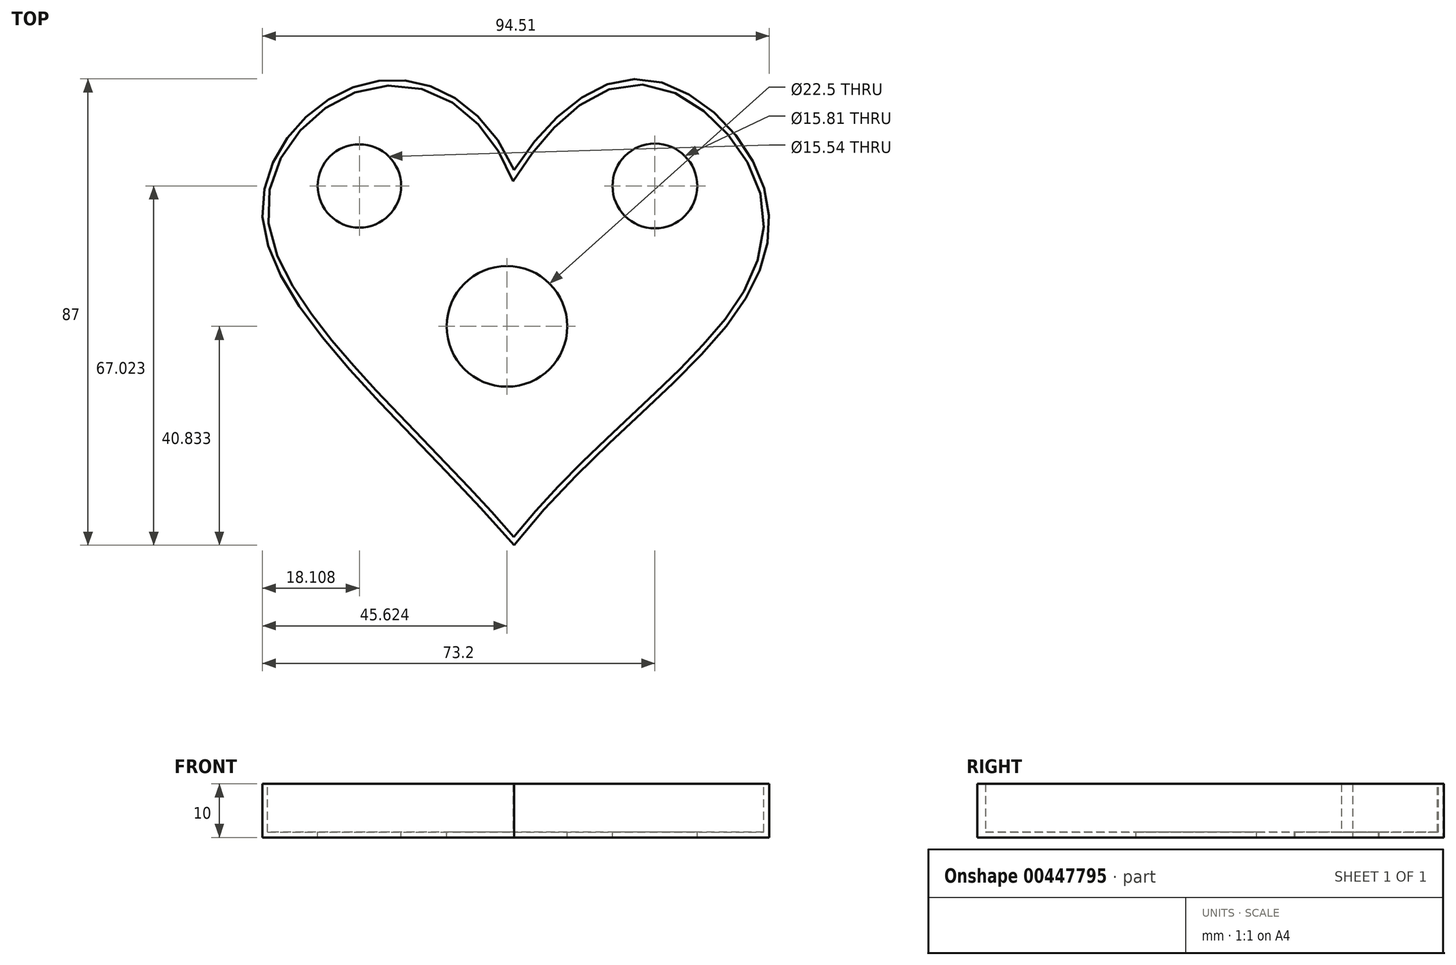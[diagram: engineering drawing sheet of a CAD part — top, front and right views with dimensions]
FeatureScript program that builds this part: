
annotation { "Feature Type Name" : "Feature", "Feature Type Description" : "" }
export const myFeature = defineFeature(function(context is Context, id is Id, definition is map)
    precondition{}
    {
        {
            var Q0;
            Q0=qCreatedBy(makeId("Top.planeOp"),FACE);
            var sketch = newSketch(context, id + "F0", { "sketchPlane" : qUnion([Q0])});
            skFitSpline(sketch, "E0", {"points": [v(0, 16.97) * mm, v(-27.58, 33.14) * mm, v(-46.93, 8.75) * mm, v(0, -53.03) * mm], "startDerivative": vector(-62.03, 140.99) * mm, "endDerivative": vector(141.18, -162.9) * mm});
            skFitSpline(sketch, "E1", {"points": [v(0, -53.03) * mm, v(41.9, -9.02) * mm, v(45.6, 16.44) * mm, v(23.86, 33.94) * mm, v(0, 16.97) * mm], "startDerivative": vector(122.52, 158.56) * mm, "endDerivative": vector(-83.12, -128.15) * mm});
            skSolve(sketch);
        }
        {
            var Q0;
            Q0=makeQuery(id+"F0.imprint","IMPRINT",FACE,{"disambiguationData":[TD([[makeQuery(id+"F0.imprint","IMPRINT",EDGE,{"derivedFrom":sQuery(id+"F0.wireOp",EDGE,"E0")}),1.0]])]});
            extrude(context, id + "F1", {"entities" : qUnion([Q0]), "depth" : 10 * mm});
        }
        {
            var Q0;
            Q0=makeQuery(id+"F1.opExtrude","CAP_FACE",FACE,{"disambiguationData":[OSD([sQuery(id+"F0.wireOp",EDGE,"E0"),sQuery(id+"F0.wireOp",EDGE,"E1")])],"isStart":false});
            shell(context, id + "F2", {"entities" : qUnion([Q0]), "thickness" : 1 * mm});
        }
        {
            var Q0;
            Q0=makeQuery(id+"F2.opShell","OFFSET_FACE",FACE,{"disambiguationData":[OSD([sQuery(id+"F0.wireOp",EDGE,"E0"),sQuery(id+"F0.wireOp",EDGE,"E1")])]});
            var sketch = newSketch(context, id + "F3", { "sketchPlane" : qUnion([Q0])});
            skCircle(sketch, "E2", {"center": v(-28.84, 14) * mm, "radius": 7.77 * mm});
            skCircle(sketch, "E3", {"center": v(-1.33, -12.2) * mm, "radius": 11.25 * mm});
            skCircle(sketch, "E4", {"center": v(26.25, 14) * mm, "radius": 7.9 * mm});
            skSolve(sketch);
        }
        {
            var Q0;
            Q0=makeQuery(id+"F3.imprint","IMPRINT",FACE,{"disambiguationData":[TD([[makeQuery(id+"F3.imprint","IMPRINT",EDGE,{"derivedFrom":sQuery(id+"F3.wireOp",EDGE,"E2")}),1.0]])]});
            var Q1;
            Q1=makeQuery(id+"F3.imprint","IMPRINT",FACE,{"disambiguationData":[TD([[makeQuery(id+"F3.imprint","IMPRINT",EDGE,{"derivedFrom":sQuery(id+"F3.wireOp",EDGE,"E4")}),1.0]])]});
            var Q2;
            Q2=makeQuery(id+"F3.imprint","IMPRINT",FACE,{"disambiguationData":[TD([[makeQuery(id+"F3.imprint","IMPRINT",EDGE,{"derivedFrom":sQuery(id+"F3.wireOp",EDGE,"E3")}),1.0]])]});
            extrude(context, id + "F4", {"entities" : qUnion([Q0, Q1, Q2]), "operationType" : NewBodyOperationType.REMOVE, "oppositeDirection" : true, "depth" : 25 * mm});
        }
    });
